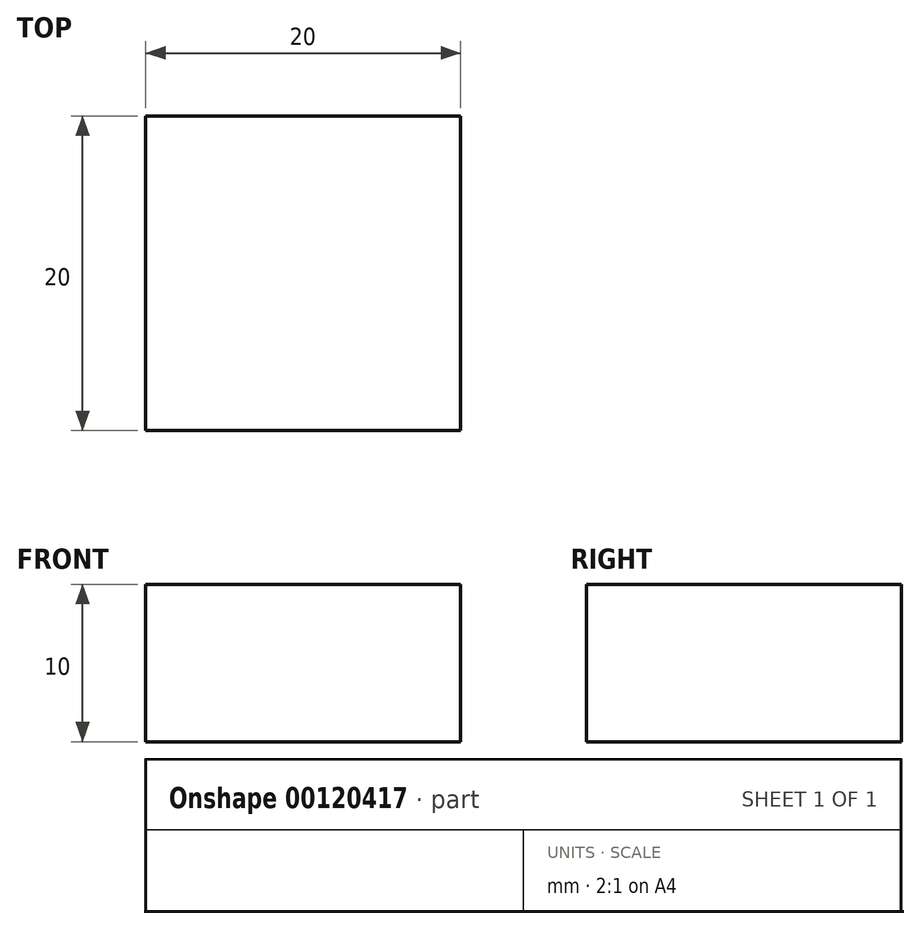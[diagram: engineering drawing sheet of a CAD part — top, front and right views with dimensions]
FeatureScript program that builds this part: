
annotation { "Feature Type Name" : "Feature", "Feature Type Description" : "" }
export const myFeature = defineFeature(function(context is Context, id is Id, definition is map)
    precondition{}
    {
        {
            var Q0;
            Q0=qCreatedBy(makeId("Top.planeOp"),FACE);
            var sketch = newSketch(context, id + "F0", { "sketchPlane" : qUnion([Q0])});
            skLineSegment(sketch, "E0.bottom", {"start": v(10, -10) * mm, "end": v(-10, -10) * mm});
            skLineSegment(sketch, "E0.top", {"start": v(10, 10) * mm, "end": v(-10, 10) * mm});
            skLineSegment(sketch, "E0.left", {"start": v(10, -10) * mm, "end": v(10, 10) * mm});
            skLineSegment(sketch, "E0.right", {"start": v(-10, -10) * mm, "end": v(-10, 10) * mm});
            skPoint(sketch, "E0.middle", {"position": v(0, 0) * mm});
            skSolve(sketch);
        }
        {
            var Q0;
            Q0=makeQuery(id+"F0.imprint","IMPRINT",FACE,{"disambiguationData":[TD([[makeQuery(id+"F0.imprint","IMPRINT",EDGE,{"derivedFrom":sQuery(id+"F0.wireOp",EDGE,"E0.bottom")}),-1.0]])]});
            extrude(context, id + "F1", {"entities" : qUnion([Q0]), "depth" : 10 * mm});
        }
    });
